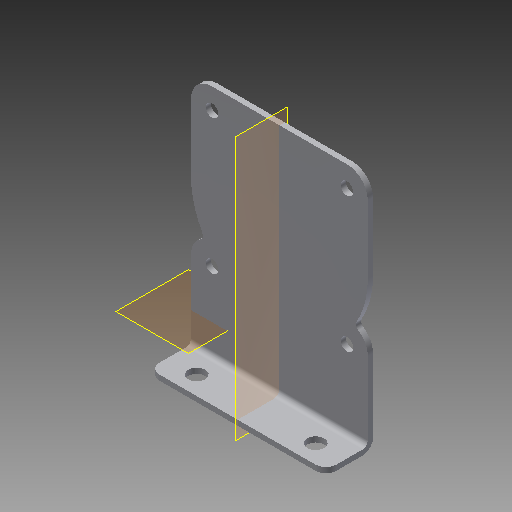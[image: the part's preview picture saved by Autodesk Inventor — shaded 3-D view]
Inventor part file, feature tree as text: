
AUTODESK INVENTOR PART (.ipt)
format: ipt  version: 2018.2 (Build 222227000, 227)  size: 187,392 bytes
history: native  units: in
note: dims shown in document units (in); Inventor stores cm internally (conversion verified against a paired STEP export)
features: sketch x6, extrude x4, fillet x3, hole x2, reference x2, plane x1, mirror x1
ambient origin geometry x8: Origin, YZ Plane, XZ Plane, XY Plane, X Axis, Y Axis, Z Axis, Center Point
bodies: Solid1 (feature_tree)
feature tree (19):
  extrude  "Extrusion1"  Depth=2.11in
  extrude  "Extrusion5"  Depth=2.11in
  extrude  "Extrusion2"  Depth=0.5in TaperAngle=0.0deg
  extrude  "Extrusion4"  Depth=0.25in TaperAngle=0.0deg
  hole  "Hole3"  [1 undecoded]
  plane  "Work Plane1"
  fillet  "Fillet3"  Radius=0.063in
  fillet  "Fillet4"  Radius=0.125in
  fillet  "Fillet5"  Radius=0.125in
  hole  "Hole6"  [1 undecoded]
  mirror  "Mirror1"
  sketch  "Sketch1"  dims[d0=2.11in d1=2.5in]
  sketch  "Sketch2"  dims[d2=0.0625in d3=0.0in d4=2.11in]
  sketch  "Sketch6"  dims[d6=0.5in d7=0.0in d29=1.0in d30=0.0in]
  reference  "Reference2"
  sketch  "Sketch7"  dims[d31=0.15in d32=0.75in d33=0.279in d34=0.25in d35=0.5635in d36=1.0in d37=0.8108in d57=1.0in d58=0.0in]
  sketch  "Sketch9"  dims[d59=0.063in d60=2.856in d61=0.063in d62=0.125in d63=0.125in]
  sketch  "Sketch10"  dims[d64=0.201in d65=0.75in d66=0.385in d67=0.25in d68=0.5635in d69=1.0in d70=0.8108in]
  reference  "Reference3"
note: 2 required parameter values undecoded (feature->parameter linkage not recoverable at this tier; creation-order binding heuristic only, values carry confidence <= 0.55)
